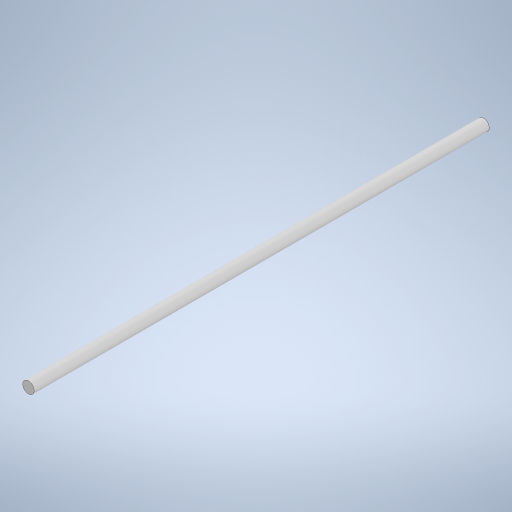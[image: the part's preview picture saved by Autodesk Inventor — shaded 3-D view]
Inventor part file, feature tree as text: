
AUTODESK INVENTOR PART (.ipt)
format: ipt  version: 2024 (Build 280153000, 153)  size: 232,960 bytes
history: native  units: mm
features: other x1, extrude x1, sketch x1
ambient origin geometry x8: Origin, YZ Plane, XZ Plane, XY Plane, X Axis, Y Axis, Z Axis, Center Point
bodies: Body1 (feature_tree)
feature tree (3):
  other  "솔리드1"
  extrude  "돌출1"  Depth=4.0mm
  sketch  "스케치1"
